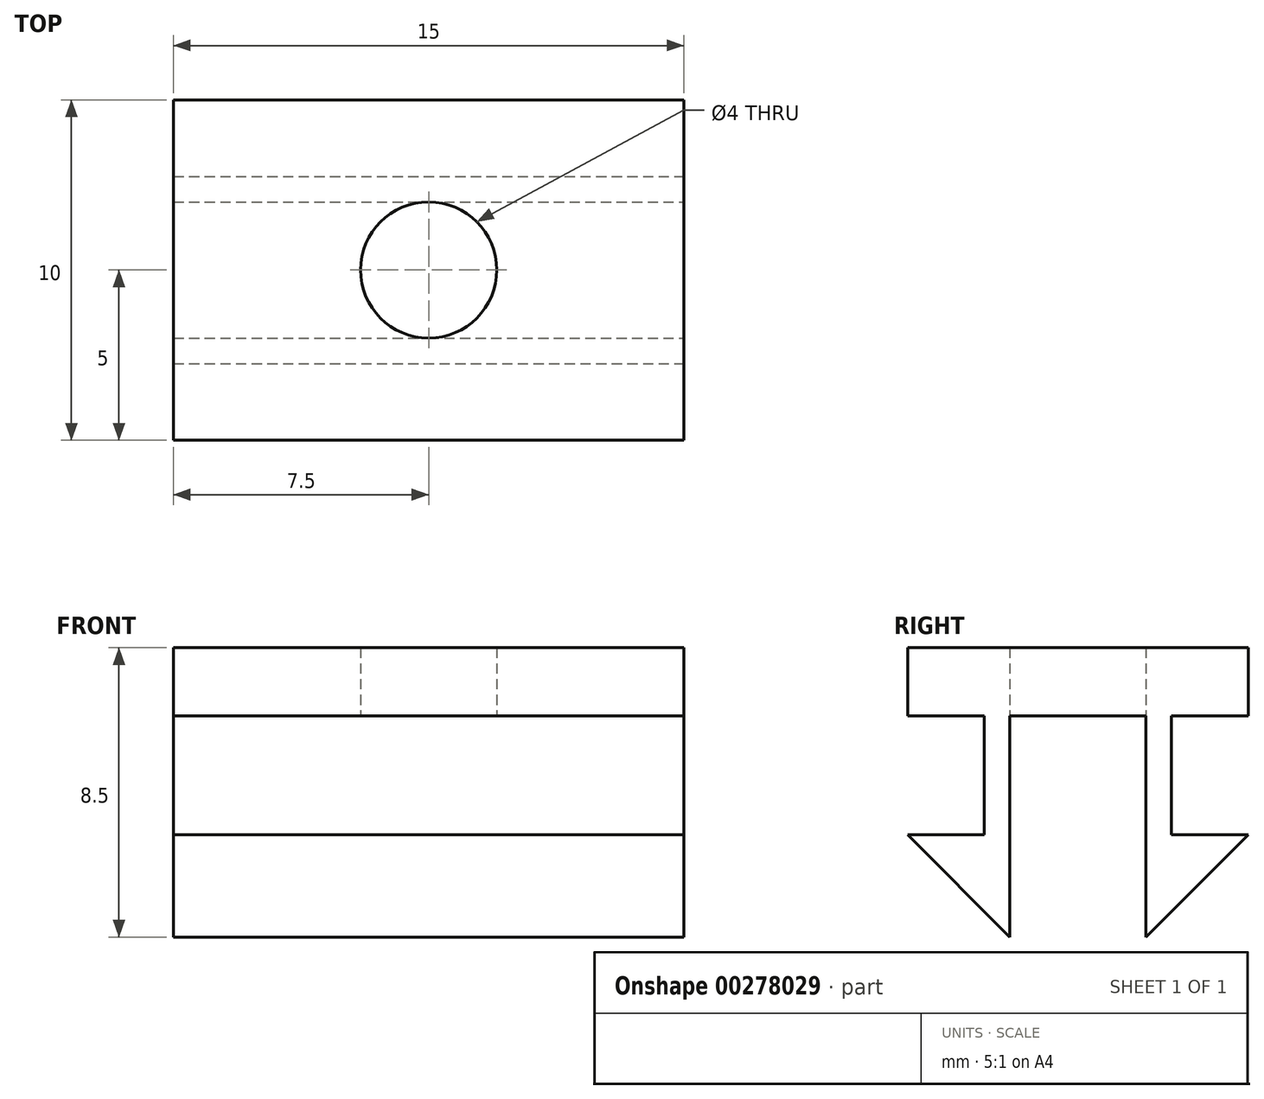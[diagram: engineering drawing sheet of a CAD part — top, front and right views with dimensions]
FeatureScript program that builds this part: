
annotation { "Feature Type Name" : "Feature", "Feature Type Description" : "" }
export const myFeature = defineFeature(function(context is Context, id is Id, definition is map)
    precondition{}
    {
        {
            var Q0;
            Q0=qCreatedBy(makeId("Top.planeOp"),FACE);
            var sketch = newSketch(context, id + "F0", { "sketchPlane" : qUnion([Q0])});
            skLineSegment(sketch, "E0.bottom", {"start": v(7.5, -5) * mm, "end": v(-7.5, -5) * mm});
            skLineSegment(sketch, "E0.top", {"start": v(7.5, 5) * mm, "end": v(-7.5, 5) * mm});
            skLineSegment(sketch, "E0.left", {"start": v(7.5, -5) * mm, "end": v(7.5, 5) * mm});
            skLineSegment(sketch, "E0.right", {"start": v(-7.5, -5) * mm, "end": v(-7.5, 5) * mm});
            skPoint(sketch, "E0.middle", {"position": v(0, 0) * mm});
            skCircle(sketch, "E1", {"center": v(0, 0) * mm, "radius": 2 * mm});
            skSolve(sketch);
        }
        {
            var Q0;
            Q0=makeQuery(id+"F0.imprint","IMPRINT",FACE,{"disambiguationData":[TD([[makeQuery(id+"F0.imprint","IMPRINT",EDGE,{"derivedFrom":sQuery(id+"F0.wireOp",EDGE,"E0.bottom")}),-1.0]])]});
            extrude(context, id + "F1", {"entities" : qUnion([Q0]), "depth" : 8.5 * mm});
        }
        {
            var Q0;
            Q0=makeQuery(id+"F1.opExtrude","SWEPT_FACE",FACE,{"disambiguationData":[OSD([sQuery(id+"F0.wireOp",EDGE,"E0.left")])]});
            var sketch = newSketch(context, id + "F2", { "sketchPlane" : qUnion([Q0])});
            skLineSegment(sketch, "E2.bottom", {"start": v(-2, 0) * mm, "end": v(2, 0) * mm});
            skLineSegment(sketch, "E2.top", {"start": v(-2, 6.5) * mm, "end": v(2, 6.5) * mm});
            skLineSegment(sketch, "E2.left", {"start": v(-2, 0) * mm, "end": v(-2, 6.5) * mm});
            skLineSegment(sketch, "E2.right", {"start": v(2, 0) * mm, "end": v(2, 6.5) * mm});
            skPoint(sketch, "E2.middle", {"position": v(0, 3.25) * mm});
            skLineSegment(sketch, "E3", {"start": v(2, 0) * mm, "end": v(5, 3) * mm});
            skPoint(sketch, "E4.endSnap0", {"position": v(5, 4.25) * mm});
            skLineSegment(sketch, "E5.MirrorCS", {"start": v(-2, 0) * mm, "end": v(-5, 3) * mm});
            skLineSegment(sketch, "E6", {"start": v(5, 3) * mm, "end": v(2.75, 3) * mm});
            skLineSegment(sketch, "E7", {"start": v(2.75, 3) * mm, "end": v(2.75, 6.5) * mm});
            skLineSegment(sketch, "E8", {"start": v(2.75, 6.5) * mm, "end": v(5, 6.5) * mm});
            skLineSegment(sketch, "E9.MirrorCS", {"start": v(-5, 3) * mm, "end": v(-2.75, 3) * mm});
            skLineSegment(sketch, "E10.MirrorCS", {"start": v(-2.75, 3) * mm, "end": v(-2.75, 6.5) * mm});
            skLineSegment(sketch, "E11.MirrorCS", {"start": v(-2.75, 6.5) * mm, "end": v(-5, 6.5) * mm});
            skSolve(sketch);
        }
        {
            var Q0;
            {var subQ0=sQuery(id+"F2.wireOp",EDGE,"E3");Q0=makeQuery(id+"F2.imprint","IMPRINT",FACE,{"disambiguationData":[TD([[makeQuery(id+"F2.imprint","IMPRINT",EDGE,{"derivedFrom":subQ0}),-1.0]])]});}
            var Q1;
            {var subQ0=sQuery(id+"F2.wireOp",EDGE,"E6");Q1=makeQuery(id+"F2.imprint","IMPRINT",FACE,{"disambiguationData":[TD([[makeQuery(id+"F2.imprint","IMPRINT",EDGE,{"derivedFrom":subQ0}),-1.0]])]});}
            var Q2;
            {var subQ0=sQuery(id+"F2.wireOp",EDGE,"E9.MirrorCS");Q2=makeQuery(id+"F2.imprint","IMPRINT",FACE,{"disambiguationData":[TD([[makeQuery(id+"F2.imprint","IMPRINT",EDGE,{"derivedFrom":subQ0}),1.0]])]});}
            var Q3;
            {var subQ0=sQuery(id+"F2.wireOp",EDGE,"E5.MirrorCS");Q3=makeQuery(id+"F2.imprint","IMPRINT",FACE,{"disambiguationData":[TD([[makeQuery(id+"F2.imprint","IMPRINT",EDGE,{"derivedFrom":subQ0}),1.0]])]});}
            extrude(context, id + "F3", {"entities" : qUnion([Q0, Q1, Q2, Q3]), "operationType" : NewBodyOperationType.REMOVE, "oppositeDirection" : true, "depth" : 25 * mm});
        }
        {
            var Q0;
            {var subQ0=sQuery(id+"F0.wireOp",EDGE,"E0.left");var subQ1=sQuery(id+"F0.wireOp",EDGE,"E1");Q0=makeQuery(id+"F3.boolean.opBoolean","SPLIT",FACE,{"disambiguationData":[TD([makeQuery(id+"F1.opExtrude","SWEPT_FACE",FACE,{"disambiguationData":[OSD([subQ0])]})])],"derivedFrom":makeQuery(id+"F1.opExtrude","CAP_FACE",FACE,{"disambiguationData":[OSD([sQuery(id+"F0.wireOp",EDGE,"E0.bottom"),sQuery(id+"F0.wireOp",EDGE,"E0.top"),subQ0,sQuery(id+"F0.wireOp",EDGE,"E0.right"),subQ1])],"isStart":true})});}
            var Q1;
            {var subQ0=sQuery(id+"F0.wireOp",EDGE,"E0.right");var subQ1=sQuery(id+"F0.wireOp",EDGE,"E1");Q1=makeQuery(id+"F3.boolean.opBoolean","SPLIT",FACE,{"disambiguationData":[TD([makeQuery(id+"F1.opExtrude","SWEPT_FACE",FACE,{"disambiguationData":[OSD([subQ0])]})])],"derivedFrom":makeQuery(id+"F1.opExtrude","CAP_FACE",FACE,{"disambiguationData":[OSD([sQuery(id+"F0.wireOp",EDGE,"E0.bottom"),sQuery(id+"F0.wireOp",EDGE,"E0.top"),sQuery(id+"F0.wireOp",EDGE,"E0.left"),subQ0,subQ1])],"isStart":true})});}
            extrude(context, id + "F4", {"entities" : qUnion([Q0, Q1]), "operationType" : NewBodyOperationType.REMOVE, "oppositeDirection" : true, "depth" : 6.5 * mm});
        }
    });
